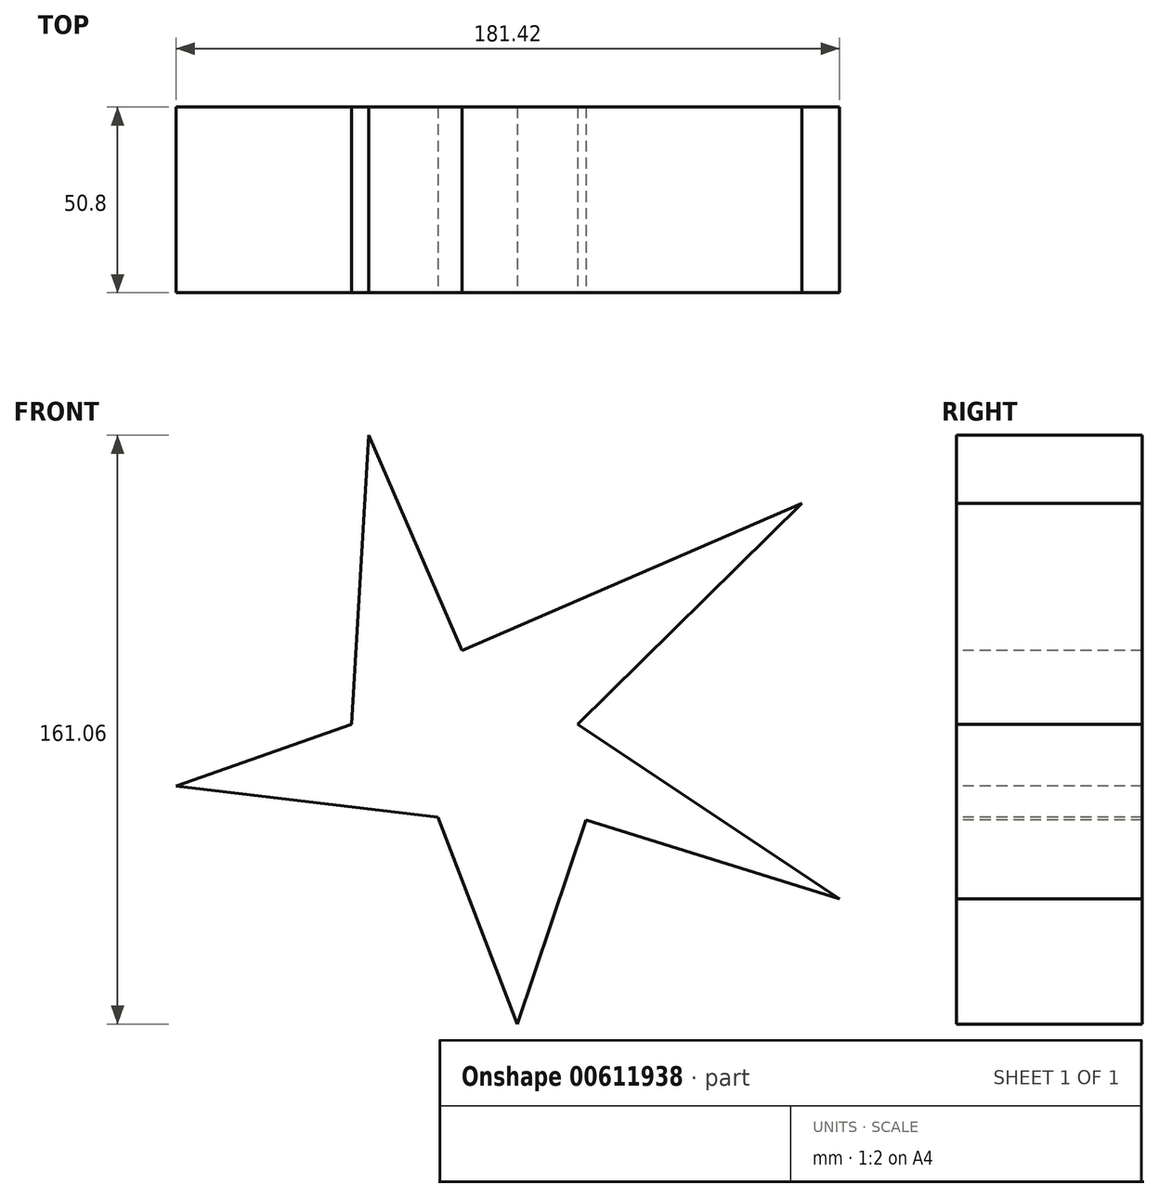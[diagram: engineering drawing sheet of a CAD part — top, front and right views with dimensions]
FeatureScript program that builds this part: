
annotation { "Feature Type Name" : "Feature", "Feature Type Description" : "" }
export const myFeature = defineFeature(function(context is Context, id is Id, definition is map)
    precondition{}
    {
        {
            var Q0;
            Q0=qCreatedBy(makeId("Front.planeOp"),FACE);
            var sketch = newSketch(context, id + "F0", { "sketchPlane" : qUnion([Q0])});
            skLineSegment(sketch, "E0", {"start": v(0, 0) * mm, "end": v(71.58, -22.3) * mm});
            skLineSegment(sketch, "E1", {"start": v(71.58, -22.3) * mm, "end": v(0, 25.45) * mm});
            skLineSegment(sketch, "E2", {"start": v(0, 25.45) * mm, "end": v(61.3, 85.95) * mm});
            skLineSegment(sketch, "E3", {"start": v(61.3, 85.95) * mm, "end": v(-31.66, 45.65) * mm});
            skLineSegment(sketch, "E4", {"start": v(-31.66, 45.65) * mm, "end": v(-57.2, 104.53) * mm});
            skLineSegment(sketch, "E5", {"start": v(-57.2, 104.53) * mm, "end": v(-61.83, 25.45) * mm});
            skLineSegment(sketch, "E6", {"start": v(-61.83, 25.45) * mm, "end": v(-109.84, 8.57) * mm});
            skLineSegment(sketch, "E7", {"start": v(-109.84, 8.57) * mm, "end": v(-38.28, 0) * mm});
            skLineSegment(sketch, "E8", {"start": v(266.6, -90.44) * mm, "end": v(275.67, -123.07) * mm});
            skLineSegment(sketch, "E9", {"start": v(-38.28, 0) * mm, "end": v(-16.57, -56.53) * mm});
            skLineSegment(sketch, "E10", {"start": v(-16.57, -56.53) * mm, "end": v(2.2, -0.69) * mm});
            skLineSegment(sketch, "E11", {"start": v(2.2, -0.69) * mm, "end": v(0, -7.26) * mm});
            skSolve(sketch);
        }
        {
            var Q0;
            {var subQ0=sQuery(id+"F0.wireOp",EDGE,"E1");Q0=makeQuery(id+"F0.imprint","IMPRINT",FACE,{"disambiguationData":[TD([[makeQuery(id+"F0.imprint","IMPRINT",EDGE,{"derivedFrom":subQ0}),1.0]])]});}
            extrude(context, id + "F1", {"entities" : qUnion([Q0]), "endBound" : BoundingType.SYMMETRIC, "oppositeDirection" : true, "depth" : 50.8 * mm, "offsetDistance" : 25.4 * mm});
        }
    });
